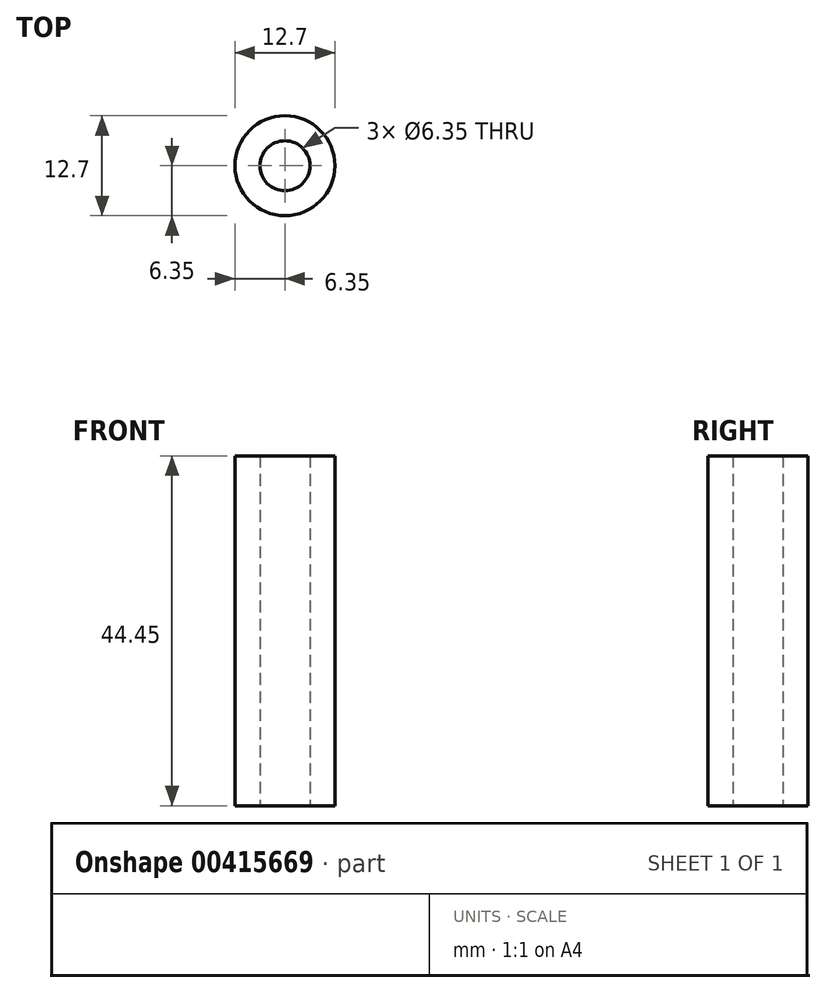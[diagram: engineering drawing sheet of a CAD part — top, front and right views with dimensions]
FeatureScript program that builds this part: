
annotation { "Feature Type Name" : "Feature", "Feature Type Description" : "" }
export const myFeature = defineFeature(function(context is Context, id is Id, definition is map)
    precondition{}
    {
        {
            var Q0;
            Q0=qCreatedBy(makeId("Top.planeOp"),FACE);
            var sketch = newSketch(context, id + "F0", { "sketchPlane" : qUnion([Q0])});
            skCircle(sketch, "E0", {"center": v(0, 0) * mm, "radius": 6.35 * mm});
            skCircle(sketch, "E1", {"center": v(0, 0) * mm, "radius": 3.18 * mm});
            skSolve(sketch);
        }
        {
            var Q0;
            Q0=makeQuery(id+"F0.imprint","IMPRINT",FACE,{"disambiguationData":[TD([[makeQuery(id+"F0.imprint","IMPRINT",EDGE,{"derivedFrom":sQuery(id+"F0.wireOp",EDGE,"E0")}),1.0]])]});
            extrude(context, id + "F1", {"entities" : qUnion([Q0]), "depth" : 44.45 * mm});
        }
    });
